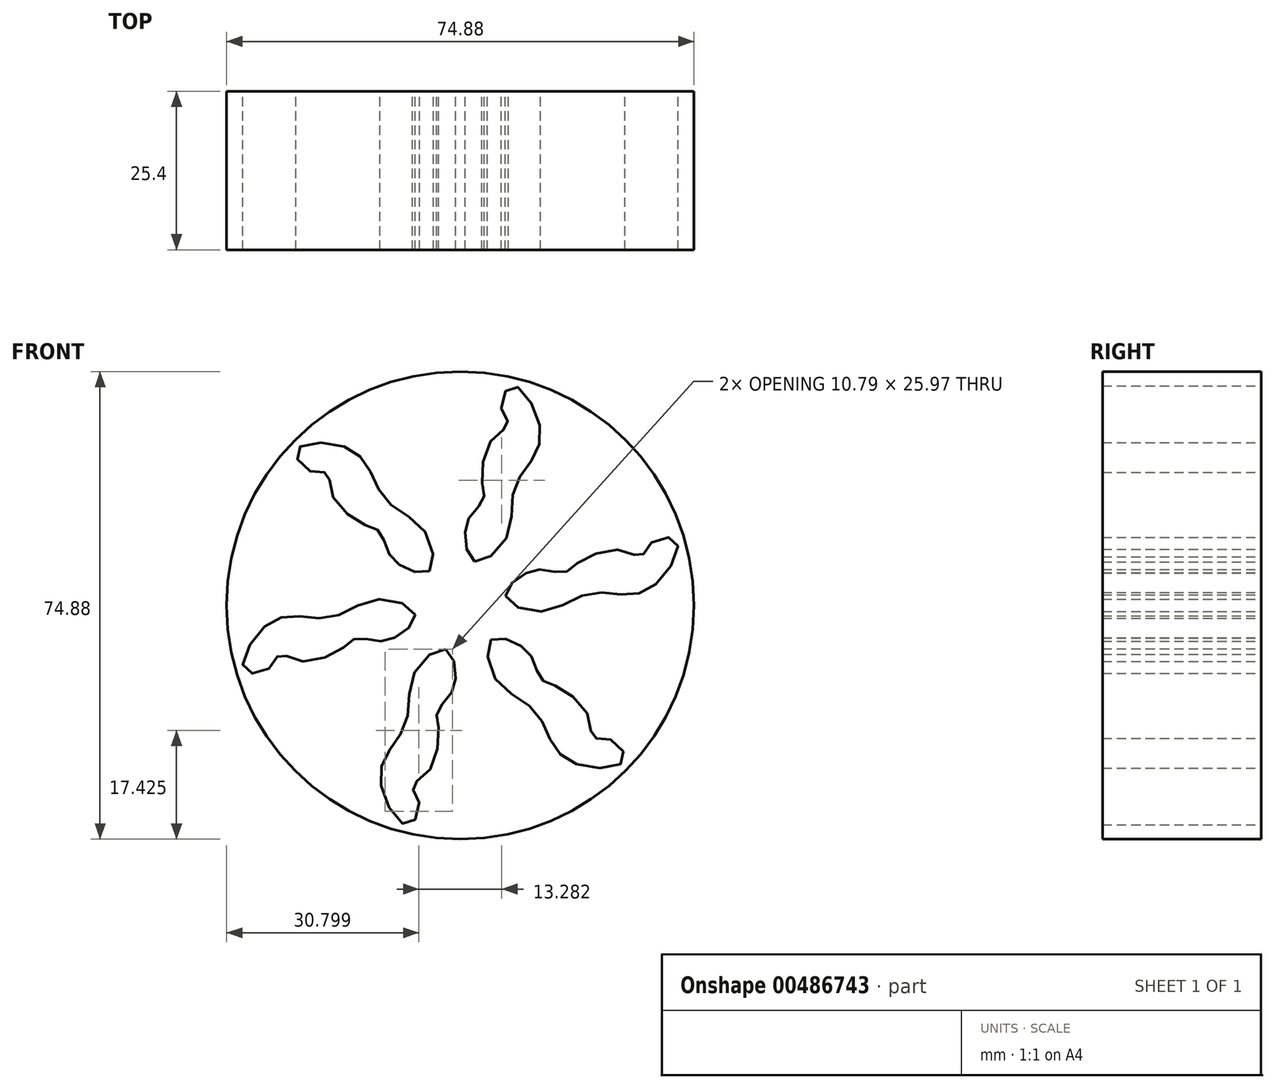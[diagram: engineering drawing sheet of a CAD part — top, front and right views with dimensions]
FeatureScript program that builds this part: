
annotation { "Feature Type Name" : "Feature", "Feature Type Description" : "" }
export const myFeature = defineFeature(function(context is Context, id is Id, definition is map)
    precondition{}
    {
        {
            var Q0;
            Q0=qCreatedBy(makeId("Front.planeOp"),FACE);
            var sketch = newSketch(context, id + "F0", { "sketchPlane" : qUnion([Q0])});
            skCircle(sketch, "E0", {"center": v(0, 0) * mm, "radius": 37.44 * mm});
            skSolve(sketch);
        }
        {
            var Q0;
            Q0=makeQuery(id+"F0.imprint","IMPRINT",FACE,{"disambiguationData":[TD([[makeQuery(id+"F0.imprint","IMPRINT",EDGE,{"derivedFrom":sQuery(id+"F0.wireOp",EDGE,"E0")}),1.0]])]});
            extrude(context, id + "F1", {"entities" : qUnion([Q0]), "depth" : 25.4 * mm});
        }
        {
            var Q0;
            Q0=makeQuery(id+"F1.opExtrude","CAP_FACE",FACE,{"disambiguationData":[OSD([sQuery(id+"F0.wireOp",EDGE,"E0")])],"isStart":false});
            var sketch = newSketch(context, id + "F2", { "sketchPlane" : qUnion([Q0])});
            skLineSegment(sketch, "E1", {"start": v(0, 0) * mm, "end": v(0, 0) * mm});
            skLineSegment(sketch, "E2", {"start": v(-28.45, 24.34) * mm, "end": v(-28.43, 24.36) * mm});
            skFitSpline(sketch, "E3", {"points": [v(-4.93, 5.52) * mm, v(-5.74, 11.92) * mm, v(-11.84, 16.8) * mm, v(-14.88, 22.38) * mm, v(-19.65, 25.73) * mm, v(-26.25, 24.81) * mm, v(-24.02, 21.46) * mm, v(-21.28, 21.16) * mm, v(-20.47, 17.6) * mm, v(-14.98, 12.73) * mm, v(-12.85, 11.72) * mm, v(-11.53, 8.47) * mm, v(-8.9, 6.03) * mm, v(-4.93, 5.52) * mm]});
            skSolve(sketch);
        }
        {
            var Q0;
            Q0=qCreatedBy(makeId("Top.planeOp"),FACE);
            var sketch = newSketch(context, id + "F3", { "sketchPlane" : qUnion([Q0])});
            skLineSegment(sketch, "E4", {"start": v(0, -47.57) * mm, "end": v(0, 16.34) * mm, "construction": true});
            skSolve(sketch);
        }
        {
            var Q0;
            Q0=makeQuery(id+"F2.imprint","IMPRINT",FACE,{"disambiguationData":[TD([[makeQuery(id+"F2.imprint","IMPRINT",EDGE,{"derivedFrom":sQuery(id+"F2.wireOp",EDGE,"E3")}),1.0]])]});
            extrude(context, id + "F4", {"entities" : qUnion([Q0]), "oppositeDirection" : true, "depth" : 59.74 * mm});
        }
        {
            var Q0;
            Q0=makeQuery(id+"F4.opExtrude","SWEPT_BODY",BODY,{"disambiguationData":[OSD([sQuery(id+"F2.wireOp",EDGE,"E3")])]});
            var Q1;
            Q1=sQuery(id+"F3.wireOp",EDGE,"E4");
            circularPattern(context, id + "F5", {"entities" : qUnion([Q0]), "axis" : qUnion([Q1]), "angle" : 360 * degree, "instanceCount" : 6, "equalSpace" : true});
        }
        {
            var Q0;
            Q0=makeQuery(id+"F4.opExtrude","SWEPT_BODY",BODY,{"disambiguationData":[OSD([sQuery(id+"F2.wireOp",EDGE,"E3")])]});
            var Q1;
            Q1=makeQuery(id+"F5.opPattern","COPY",BODY,{"derivedFrom":makeQuery(id+"F4.opExtrude","SWEPT_BODY",BODY,{"disambiguationData":[OSD([sQuery(id+"F2.wireOp",EDGE,"E3")])]}),"instanceName":"1"});
            var Q2;
            Q2=makeQuery(id+"F5.opPattern","COPY",BODY,{"derivedFrom":makeQuery(id+"F4.opExtrude","SWEPT_BODY",BODY,{"disambiguationData":[OSD([sQuery(id+"F2.wireOp",EDGE,"E3")])]}),"instanceName":"2"});
            var Q3;
            Q3=makeQuery(id+"F5.opPattern","COPY",BODY,{"derivedFrom":makeQuery(id+"F4.opExtrude","SWEPT_BODY",BODY,{"disambiguationData":[OSD([sQuery(id+"F2.wireOp",EDGE,"E3")])]}),"instanceName":"3"});
            var Q4;
            Q4=makeQuery(id+"F5.opPattern","COPY",BODY,{"derivedFrom":makeQuery(id+"F4.opExtrude","SWEPT_BODY",BODY,{"disambiguationData":[OSD([sQuery(id+"F2.wireOp",EDGE,"E3")])]}),"instanceName":"4"});
            var Q5;
            Q5=makeQuery(id+"F5.opPattern","COPY",BODY,{"derivedFrom":makeQuery(id+"F4.opExtrude","SWEPT_BODY",BODY,{"disambiguationData":[OSD([sQuery(id+"F2.wireOp",EDGE,"E3")])]}),"instanceName":"5"});
            var Q6;
            Q6=makeQuery(id+"F1.opExtrude","SWEPT_BODY",BODY,{"disambiguationData":[OSD([sQuery(id+"F0.wireOp",EDGE,"E0")])]});
            booleanBodies(context, id + "F6", {"operationType" : BooleanOperationType.SUBTRACTION, "tools" : qUnion([Q0, Q1, Q2, Q3, Q4, Q5]), "targets" : qUnion([Q6])});
        }
    });
